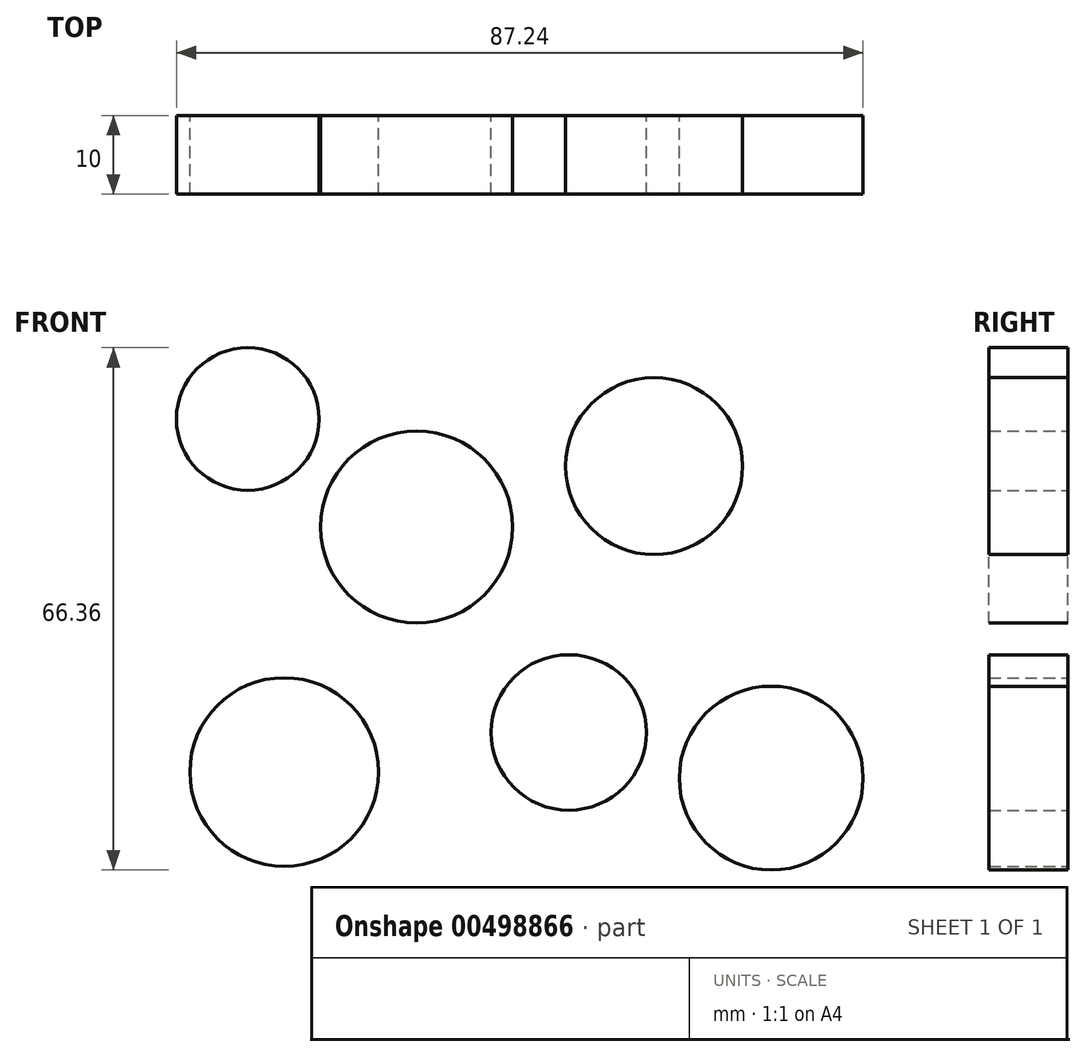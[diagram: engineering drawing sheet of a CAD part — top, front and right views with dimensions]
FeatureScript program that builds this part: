
annotation { "Feature Type Name" : "Feature", "Feature Type Description" : "" }
export const myFeature = defineFeature(function(context is Context, id is Id, definition is map)
    precondition{}
    {
        {
            var Q0;
            Q0=qCreatedBy(makeId("Front.planeOp"),FACE);
            var sketch = newSketch(context, id + "F0", { "sketchPlane" : qUnion([Q0])});
            skLineSegment(sketch, "E0.bottom", {"start": v(43.3, -34.94) * mm, "end": v(-55.73, -34.94) * mm});
            skLineSegment(sketch, "E0.top", {"start": v(43.3, 56.86) * mm, "end": v(-55.73, 56.86) * mm});
            skLineSegment(sketch, "E0.left", {"start": v(43.3, -34.94) * mm, "end": v(43.3, 56.86) * mm});
            skLineSegment(sketch, "E0.right", {"start": v(-55.73, -34.94) * mm, "end": v(-55.73, 56.86) * mm});
            skCircle(sketch, "E1", {"center": v(-17.97, 17.18) * mm, "radius": 12.2 * mm});
            skCircle(sketch, "E2", {"center": v(12.19, 24.92) * mm, "radius": 11.24 * mm});
            skCircle(sketch, "E3", {"center": v(1.36, -8.91) * mm, "radius": 9.87 * mm});
            skCircle(sketch, "E4", {"center": v(-34.79, -13.94) * mm, "radius": 11.98 * mm});
            skCircle(sketch, "E5", {"center": v(-39.43, 30.9) * mm, "radius": 9.06 * mm});
            skCircle(sketch, "E6", {"center": v(27.07, -14.71) * mm, "radius": 11.68 * mm});
            skSolve(sketch);
        }
        {
            var Q0;
            Q0=makeQuery(id+"F0.imprint","IMPRINT",FACE,{"disambiguationData":[TD([[makeQuery(id+"F0.imprint","IMPRINT",EDGE,{"derivedFrom":sQuery(id+"F0.wireOp",EDGE,"E5")}),1.0]])]});
            var Q1;
            Q1=makeQuery(id+"F0.imprint","IMPRINT",FACE,{"disambiguationData":[TD([[makeQuery(id+"F0.imprint","IMPRINT",EDGE,{"derivedFrom":sQuery(id+"F0.wireOp",EDGE,"E1")}),1.0]])]});
            var Q2;
            Q2=makeQuery(id+"F0.imprint","IMPRINT",FACE,{"disambiguationData":[TD([[makeQuery(id+"F0.imprint","IMPRINT",EDGE,{"derivedFrom":sQuery(id+"F0.wireOp",EDGE,"E2")}),1.0]])]});
            var Q3;
            Q3=makeQuery(id+"F0.imprint","IMPRINT",FACE,{"disambiguationData":[TD([[makeQuery(id+"F0.imprint","IMPRINT",EDGE,{"derivedFrom":sQuery(id+"F0.wireOp",EDGE,"E4")}),1.0]])]});
            var Q4;
            Q4=makeQuery(id+"F0.imprint","IMPRINT",FACE,{"disambiguationData":[TD([[makeQuery(id+"F0.imprint","IMPRINT",EDGE,{"derivedFrom":sQuery(id+"F0.wireOp",EDGE,"E3")}),1.0]])]});
            var Q5;
            Q5=makeQuery(id+"F0.imprint","IMPRINT",FACE,{"disambiguationData":[TD([[makeQuery(id+"F0.imprint","IMPRINT",EDGE,{"derivedFrom":sQuery(id+"F0.wireOp",EDGE,"E6")}),1.0]])]});
            extrude(context, id + "F1", {"entities" : qUnion([Q0, Q1, Q2, Q3, Q4, Q5]), "depth" : 10 * mm, "offsetDistance" : 25 * mm});
        }
    });
